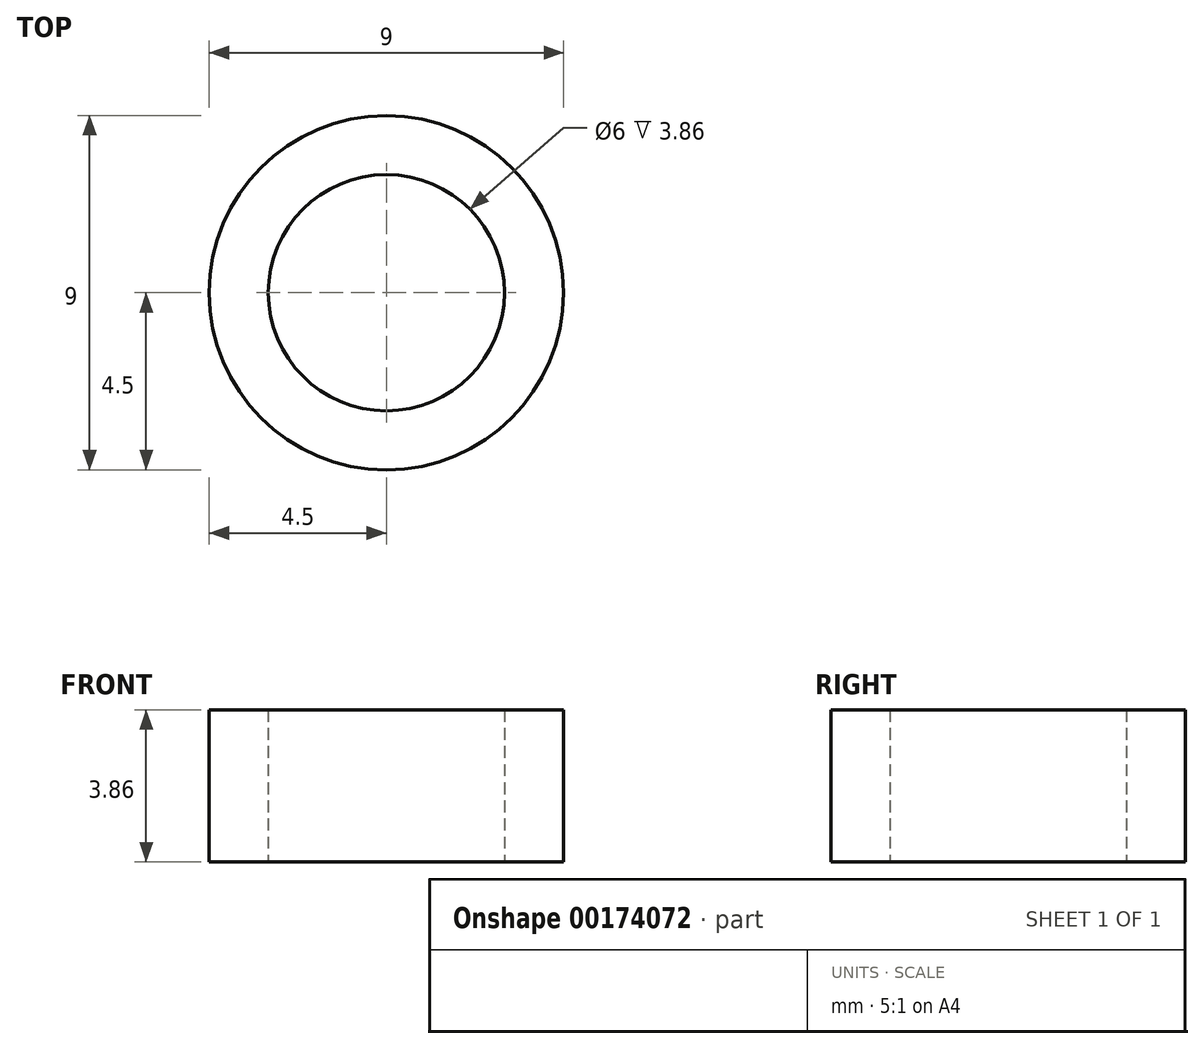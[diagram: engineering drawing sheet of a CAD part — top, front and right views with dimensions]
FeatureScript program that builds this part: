
annotation { "Feature Type Name" : "Feature", "Feature Type Description" : "" }
export const myFeature = defineFeature(function(context is Context, id is Id, definition is map)
    precondition{}
    {
        {
            var Q0;
            Q0=qCreatedBy(makeId("Top.planeOp"),FACE);
            var sketch = newSketch(context, id + "F0", { "sketchPlane" : qUnion([Q0])});
            skCircle(sketch, "E0", {"center": v(0, 0) * mm, "radius": 4.5 * mm});
            skCircle(sketch, "E1", {"center": v(0, 0) * mm, "radius": 3 * mm});
            skSolve(sketch);
        }
        {
            var Q0;
            Q0=makeQuery(id+"F0.imprint","IMPRINT",FACE,{"disambiguationData":[TD([[makeQuery(id+"F0.imprint","IMPRINT",EDGE,{"derivedFrom":sQuery(id+"F0.wireOp",EDGE,"E0")}),1.0]])]});
            extrude(context, id + "F1", {"entities" : qUnion([Q0]), "depth" : 3.86 * mm});
        }
    });
